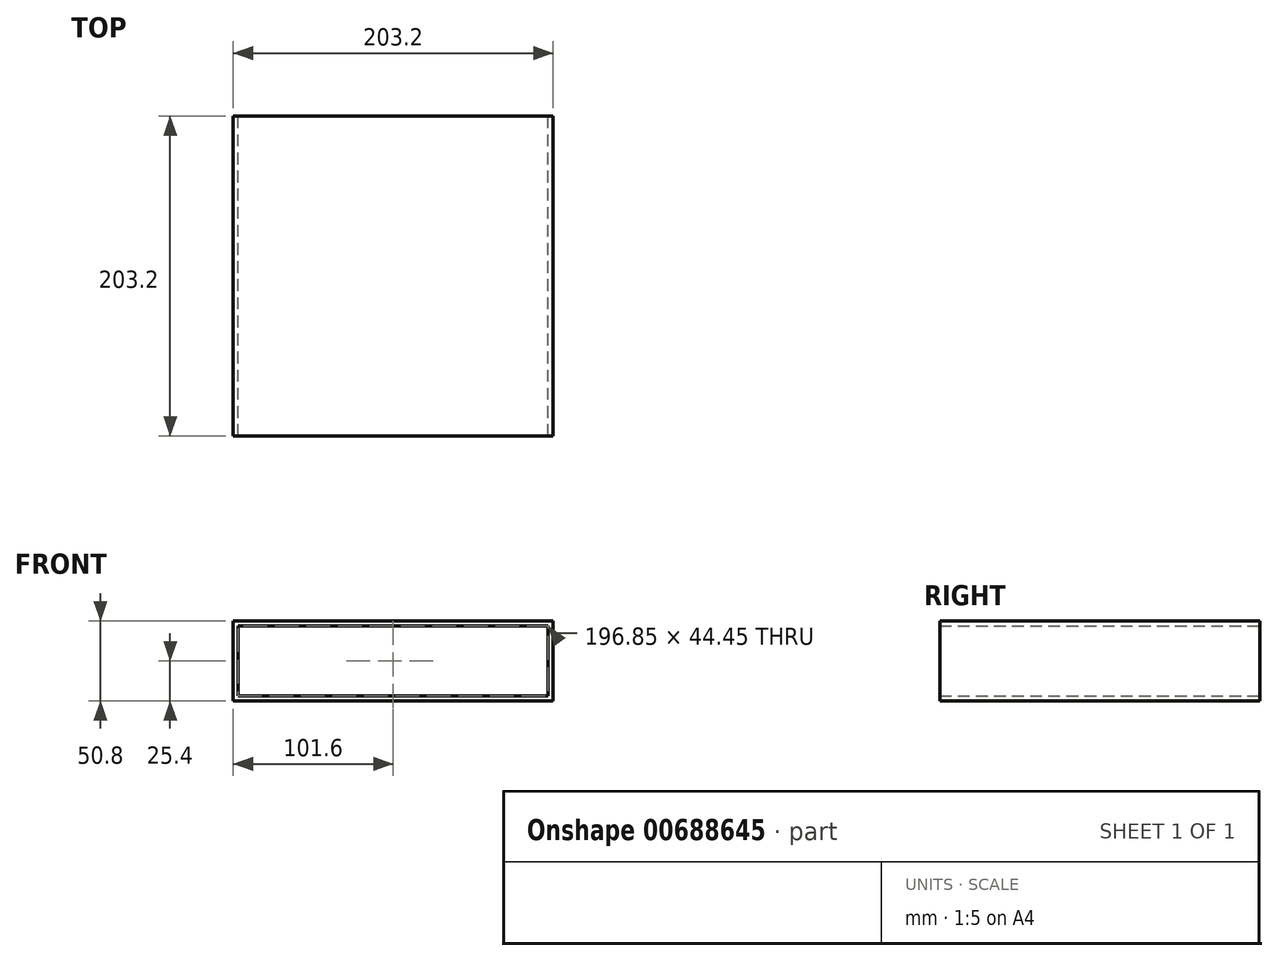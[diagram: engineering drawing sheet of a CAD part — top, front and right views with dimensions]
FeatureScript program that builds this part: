
annotation { "Feature Type Name" : "Feature", "Feature Type Description" : "" }
export const myFeature = defineFeature(function(context is Context, id is Id, definition is map)
    precondition{}
    {
        {
            var Q0;
            Q0=qCreatedBy(makeId("Front.planeOp"),FACE);
            var sketch = newSketch(context, id + "F0", { "sketchPlane" : qUnion([Q0])});
            skLineSegment(sketch, "E0.bottom", {"start": v(0, 0) * mm, "end": v(203.2, 0) * mm});
            skLineSegment(sketch, "E0.top", {"start": v(0, 50.8) * mm, "end": v(203.2, 50.8) * mm});
            skLineSegment(sketch, "E0.left", {"start": v(0, 0) * mm, "end": v(0, 50.8) * mm});
            skLineSegment(sketch, "E0.right", {"start": v(203.2, 0) * mm, "end": v(203.2, 50.8) * mm});
            skLineSegment(sketch, "E1.0", {"start": v(3.17, 47.63) * mm, "end": v(200.03, 47.63) * mm});
            skLineSegment(sketch, "E1.1", {"start": v(3.17, 3.17) * mm, "end": v(3.17, 47.63) * mm});
            skLineSegment(sketch, "E1.2", {"start": v(3.17, 3.17) * mm, "end": v(200.03, 3.17) * mm});
            skLineSegment(sketch, "E1.3", {"start": v(200.03, 3.17) * mm, "end": v(200.03, 47.63) * mm});
            skSolve(sketch);
        }
        {
            var Q0;
            Q0 = qSketchRegion(id + "F0", true);
            extrude(context, id + "F1", {"entities" : qUnion([Q0]), "depth" : 203.2 * mm, "offsetDistance" : 25.4 * mm});
        }
    });
